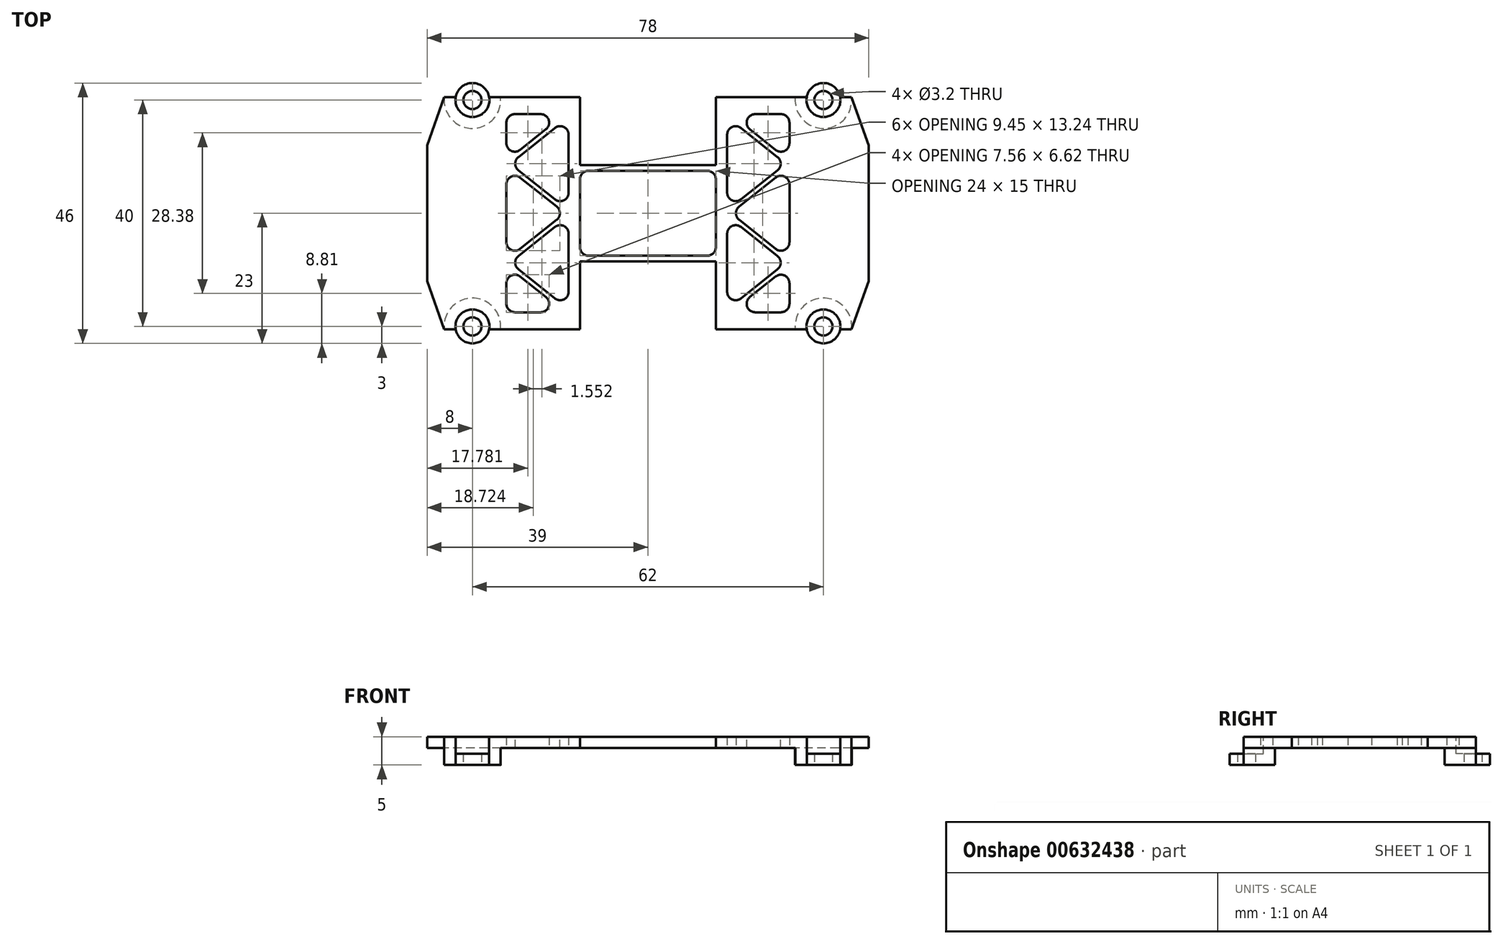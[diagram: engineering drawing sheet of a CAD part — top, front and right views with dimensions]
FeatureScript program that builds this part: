
annotation { "Feature Type Name" : "Feature", "Feature Type Description" : "" }
export const myFeature = defineFeature(function(context is Context, id is Id, definition is map)
    precondition{}
    {
        {
            var Q0;
            Q0=qCreatedBy(makeId("Top.planeOp"),FACE);
            var sketch = newSketch(context, id + "F0", { "sketchPlane" : qUnion([Q0])});
            skLineSegment(sketch, "E0.bottom", {"start": v(-31, 20) * mm, "end": v(31, 20) * mm, "construction": true});
            skLineSegment(sketch, "E0.top", {"start": v(-31, -20) * mm, "end": v(31, -20) * mm, "construction": true});
            skLineSegment(sketch, "E0.left", {"start": v(-31, 20) * mm, "end": v(-31, -20) * mm, "construction": true});
            skLineSegment(sketch, "E0.right", {"start": v(31, 20) * mm, "end": v(31, -20) * mm, "construction": true});
            skCircle(sketch, "E1", {"center": v(-31, 20) * mm, "radius": 1.6 * mm});
            skCircle(sketch, "E2", {"center": v(31, 20) * mm, "radius": 1.6 * mm});
            skCircle(sketch, "E3", {"center": v(31, -20) * mm, "radius": 1.6 * mm});
            skCircle(sketch, "E4", {"center": v(-31, -20) * mm, "radius": 1.6 * mm});
            skLineSegment(sketch, "E5.bottom", {"start": v(-39, 20.5) * mm, "end": v(39, 20.5) * mm});
            skLineSegment(sketch, "E5.top", {"start": v(-39, -20.5) * mm, "end": v(39, -20.5) * mm});
            skLineSegment(sketch, "E5.left", {"start": v(-39, 20.5) * mm, "end": v(-39, -20.5) * mm});
            skLineSegment(sketch, "E5.right", {"start": v(39, 20.5) * mm, "end": v(39, -20.5) * mm});
            skCircle(sketch, "E6", {"center": v(-31, 20) * mm, "radius": 3 * mm});
            skCircle(sketch, "E7", {"center": v(31, 20) * mm, "radius": 3 * mm});
            skCircle(sketch, "E8", {"center": v(31, -20) * mm, "radius": 3 * mm});
            skCircle(sketch, "E9", {"center": v(-31, -20) * mm, "radius": 3 * mm});
            skCircle(sketch, "E10", {"center": v(-31, 20) * mm, "radius": 5 * mm});
            skCircle(sketch, "E11", {"center": v(-31, -20) * mm, "radius": 5 * mm});
            skCircle(sketch, "E12", {"center": v(31, 20) * mm, "radius": 5 * mm});
            skCircle(sketch, "E13", {"center": v(31, -20) * mm, "radius": 5 * mm});
            skLineSegment(sketch, "E14.bottom", {"start": v(-39, 12) * mm, "end": v(-27, 12) * mm});
            skLineSegment(sketch, "E14.top", {"start": v(-39, -12) * mm, "end": v(-27, -12) * mm});
            skLineSegment(sketch, "E14.left", {"start": v(-39, 12) * mm, "end": v(-39, -12) * mm});
            skLineSegment(sketch, "E14.right", {"start": v(-27, 12) * mm, "end": v(-27, -12) * mm});
            skLineSegment(sketch, "E15.bottom", {"start": v(39, 12) * mm, "end": v(27, 12) * mm});
            skLineSegment(sketch, "E15.top", {"start": v(39, -12) * mm, "end": v(27, -12) * mm});
            skLineSegment(sketch, "E15.left", {"start": v(39, 12) * mm, "end": v(39, -12) * mm});
            skLineSegment(sketch, "E15.right", {"start": v(27, 12) * mm, "end": v(27, -12) * mm});
            skLineSegment(sketch, "E16.bottom", {"start": v(-12, 20.5) * mm, "end": v(12, 20.5) * mm});
            skLineSegment(sketch, "E16.top", {"start": v(-12, 8.5) * mm, "end": v(12, 8.5) * mm});
            skLineSegment(sketch, "E16.left", {"start": v(-12, 20.5) * mm, "end": v(-12, 8.5) * mm});
            skLineSegment(sketch, "E16.right", {"start": v(12, 20.5) * mm, "end": v(12, 8.5) * mm});
            skLineSegment(sketch, "E17.bottom", {"start": v(-12, -20.5) * mm, "end": v(12, -20.5) * mm});
            skLineSegment(sketch, "E17.top", {"start": v(-12, -8.5) * mm, "end": v(12, -8.5) * mm});
            skLineSegment(sketch, "E17.left", {"start": v(-12, -20.5) * mm, "end": v(-12, -8.5) * mm});
            skLineSegment(sketch, "E17.right", {"start": v(12, -20.5) * mm, "end": v(12, -8.5) * mm});
            skLineSegment(sketch, "E18.bottom", {"start": v(-12, 7.5) * mm, "end": v(12, 7.5) * mm});
            skLineSegment(sketch, "E18.top", {"start": v(-12, -7.5) * mm, "end": v(12, -7.5) * mm});
            skLineSegment(sketch, "E18.left", {"start": v(-12, 7.5) * mm, "end": v(-12, -7.5) * mm});
            skLineSegment(sketch, "E18.right", {"start": v(12, 7.5) * mm, "end": v(12, -7.5) * mm});
            skPoint(sketch, "E19", {"position": v(-35.97, 20.5) * mm});
            skPoint(sketch, "E20", {"position": v(-35.97, -20.5) * mm});
            skPoint(sketch, "E21", {"position": v(35.97, 20.5) * mm});
            skPoint(sketch, "E22", {"position": v(35.97, -20.5) * mm});
            skLineSegment(sketch, "E23", {"start": v(-35.97, 20.5) * mm, "end": v(-39, 12) * mm});
            skLineSegment(sketch, "E24", {"start": v(-39, -12) * mm, "end": v(-35.97, -20.5) * mm});
            skLineSegment(sketch, "E25", {"start": v(39, 12) * mm, "end": v(35.97, 20.5) * mm});
            skLineSegment(sketch, "E26", {"start": v(39, -12) * mm, "end": v(35.97, -20.5) * mm});
            skLineSegment(sketch, "E27.bottom", {"start": v(-14, 17.5) * mm, "end": v(-25, 17.5) * mm});
            skLineSegment(sketch, "E27.top", {"start": v(-14, -17.5) * mm, "end": v(-25, -17.5) * mm});
            skLineSegment(sketch, "E27.left", {"start": v(-14, 17.5) * mm, "end": v(-14, -17.5) * mm});
            skLineSegment(sketch, "E27.right", {"start": v(-25, 17.5) * mm, "end": v(-25, -17.5) * mm});
            skLineSegment(sketch, "E28.bottom", {"start": v(14, 17.5) * mm, "end": v(25, 17.5) * mm});
            skLineSegment(sketch, "E28.top", {"start": v(14, -17.5) * mm, "end": v(25, -17.5) * mm});
            skLineSegment(sketch, "E28.left", {"start": v(14, 17.5) * mm, "end": v(14, -17.5) * mm});
            skLineSegment(sketch, "E28.right", {"start": v(25, 17.5) * mm, "end": v(25, -17.5) * mm});
            skLineSegment(sketch, "E29", {"start": v(14, 0) * mm, "end": v(25, 8.75) * mm});
            skLineSegment(sketch, "E30", {"start": v(25, 8.75) * mm, "end": v(14, 17.5) * mm});
            skLineSegment(sketch, "E31", {"start": v(14, 0) * mm, "end": v(25, -8.75) * mm});
            skLineSegment(sketch, "E32", {"start": v(25, -8.75) * mm, "end": v(14, -17.5) * mm});
            skLineSegment(sketch, "E33.0", {"start": v(25.64, 8.75) * mm, "end": v(14.25, 17.81) * mm});
            skLineSegment(sketch, "E33.1", {"start": v(14.64, 0) * mm, "end": v(25.64, 8.75) * mm});
            skLineSegment(sketch, "E33.2", {"start": v(14.64, 0) * mm, "end": v(25.64, -8.75) * mm});
            skLineSegment(sketch, "E33.3", {"start": v(25.64, -8.75) * mm, "end": v(14.25, -17.81) * mm});
            skLineSegment(sketch, "E34.0", {"start": v(24.36, 8.75) * mm, "end": v(13.75, 17.19) * mm});
            skLineSegment(sketch, "E34.1", {"start": v(13.36, 0) * mm, "end": v(24.36, 8.75) * mm});
            skLineSegment(sketch, "E34.2", {"start": v(13.36, 0) * mm, "end": v(24.36, -8.75) * mm});
            skLineSegment(sketch, "E34.3", {"start": v(24.36, -8.75) * mm, "end": v(13.75, -17.19) * mm});
            skLineSegment(sketch, "E35", {"start": v(-14, 17.5) * mm, "end": v(-25, 8.75) * mm});
            skLineSegment(sketch, "E36", {"start": v(-25, 8.75) * mm, "end": v(-14, 0) * mm});
            skLineSegment(sketch, "E37", {"start": v(-14, 0) * mm, "end": v(-25, -8.75) * mm});
            skLineSegment(sketch, "E38", {"start": v(-25, -8.75) * mm, "end": v(-14, -17.5) * mm});
            skLineSegment(sketch, "E39.0", {"start": v(-24.36, -8.75) * mm, "end": v(-13.75, -17.19) * mm});
            skLineSegment(sketch, "E39.1", {"start": v(-13.36, 0) * mm, "end": v(-24.36, -8.75) * mm});
            skLineSegment(sketch, "E39.2", {"start": v(-24.36, 8.75) * mm, "end": v(-13.36, 0) * mm});
            skLineSegment(sketch, "E39.3", {"start": v(-13.75, 17.19) * mm, "end": v(-24.36, 8.75) * mm});
            skLineSegment(sketch, "E40.0", {"start": v(-25.64, -8.75) * mm, "end": v(-14.25, -17.81) * mm});
            skLineSegment(sketch, "E40.1", {"start": v(-14.64, 0) * mm, "end": v(-25.64, -8.75) * mm});
            skLineSegment(sketch, "E40.2", {"start": v(-25.64, 8.75) * mm, "end": v(-14.64, 0) * mm});
            skLineSegment(sketch, "E40.3", {"start": v(-14.25, 17.81) * mm, "end": v(-25.64, 8.75) * mm});
            skSolve(sketch);
        }
        {
            var Q0;
            {var subQ0=sQuery(id+"F0.wireOp",EDGE,"E5.top");var subQ1=sQuery(id+"F0.wireOp",EDGE,"E4");var subQ2=makeQuery(id+"F0.imprint","INTERSECT",VERTEX,{"disambiguationData":[OD(0.0)],"derivedFrom":[subQ1,subQ0]});Q0=makeQuery(id+"F0.imprint","IMPRINT",FACE,{"disambiguationData":[TD([[makeQuery(id+"F0.imprint","IMPRINT",EDGE,{"disambiguationData":[TD([[subQ2,-1.0]])],"derivedFrom":subQ1}),-1.0]])]});}
            var Q1;
            {var subQ0=sQuery(id+"F0.wireOp",EDGE,"E5.top");var subQ1=sQuery(id+"F0.wireOp",EDGE,"E4");var subQ2=makeQuery(id+"F0.imprint","INTERSECT",VERTEX,{"disambiguationData":[OD(0.0)],"derivedFrom":[subQ1,subQ0]});Q1=makeQuery(id+"F0.imprint","IMPRINT",FACE,{"disambiguationData":[TD([[makeQuery(id+"F0.imprint","IMPRINT",EDGE,{"disambiguationData":[TD([[subQ2,1.0]])],"derivedFrom":subQ1}),-1.0]])]});}
            var Q2;
            {var subQ0=sQuery(id+"F0.wireOp",EDGE,"E11");var subQ1=sQuery(id+"F0.wireOp",EDGE,"E5.top");var subQ5=makeQuery(id+"F0.imprint","INTERSECT",VERTEX,{"derivedFrom":[subQ1,subQ0]});Q2=makeQuery(id+"F0.imprint","IMPRINT",FACE,{"disambiguationData":[TD([[makeQuery(id+"F0.imprint","IMPRINT",EDGE,{"disambiguationData":[TD([[subQ5,1.0]])],"derivedFrom":subQ1}),1.0]])]});}
            var Q3;
            {var subQ0=sQuery(id+"F0.wireOp",EDGE,"E5.bottom");var subQ1=sQuery(id+"F0.wireOp",EDGE,"E1");var subQ2=makeQuery(id+"F0.imprint","INTERSECT",VERTEX,{"disambiguationData":[OD(0.0)],"derivedFrom":[subQ1,subQ0]});Q3=makeQuery(id+"F0.imprint","IMPRINT",FACE,{"disambiguationData":[TD([[makeQuery(id+"F0.imprint","IMPRINT",EDGE,{"disambiguationData":[TD([[subQ2,1.0]])],"derivedFrom":subQ1}),-1.0]])]});}
            var Q4;
            {var subQ0=sQuery(id+"F0.wireOp",EDGE,"E5.bottom");var subQ1=sQuery(id+"F0.wireOp",EDGE,"E1");var subQ2=makeQuery(id+"F0.imprint","INTERSECT",VERTEX,{"disambiguationData":[OD(0.0)],"derivedFrom":[subQ1,subQ0]});Q4=makeQuery(id+"F0.imprint","IMPRINT",FACE,{"disambiguationData":[TD([[makeQuery(id+"F0.imprint","IMPRINT",EDGE,{"disambiguationData":[TD([[subQ2,-1.0]])],"derivedFrom":subQ1}),-1.0]])]});}
            var Q5;
            {var subQ0=sQuery(id+"F0.wireOp",EDGE,"E5.bottom");var subQ1=sQuery(id+"F0.wireOp",EDGE,"E2");var subQ2=makeQuery(id+"F0.imprint","INTERSECT",VERTEX,{"disambiguationData":[OD(0.0)],"derivedFrom":[subQ1,subQ0]});Q5=makeQuery(id+"F0.imprint","IMPRINT",FACE,{"disambiguationData":[TD([[makeQuery(id+"F0.imprint","IMPRINT",EDGE,{"disambiguationData":[TD([[subQ2,1.0]])],"derivedFrom":subQ1}),-1.0]])]});}
            var Q6;
            {var subQ0=sQuery(id+"F0.wireOp",EDGE,"E5.bottom");var subQ1=sQuery(id+"F0.wireOp",EDGE,"E2");var subQ2=makeQuery(id+"F0.imprint","INTERSECT",VERTEX,{"disambiguationData":[OD(0.0)],"derivedFrom":[subQ1,subQ0]});Q6=makeQuery(id+"F0.imprint","IMPRINT",FACE,{"disambiguationData":[TD([[makeQuery(id+"F0.imprint","IMPRINT",EDGE,{"disambiguationData":[TD([[subQ2,-1.0]])],"derivedFrom":subQ1}),-1.0]])]});}
            var Q7;
            {var subQ0=sQuery(id+"F0.wireOp",EDGE,"E12");var subQ1=sQuery(id+"F0.wireOp",EDGE,"E5.bottom");var subQ2=makeQuery(id+"F0.imprint","INTERSECT",VERTEX,{"derivedFrom":[subQ1,subQ0]});Q7=makeQuery(id+"F0.imprint","IMPRINT",FACE,{"disambiguationData":[TD([[makeQuery(id+"F0.imprint","IMPRINT",EDGE,{"disambiguationData":[TD([[subQ2,-1.0]])],"derivedFrom":subQ1}),-1.0]])]});}
            var Q8;
            {var subQ0=sQuery(id+"F0.wireOp",EDGE,"E10");var subQ1=sQuery(id+"F0.wireOp",EDGE,"E5.bottom");var subQ5=makeQuery(id+"F0.imprint","INTERSECT",VERTEX,{"derivedFrom":[subQ1,subQ0]});Q8=makeQuery(id+"F0.imprint","IMPRINT",FACE,{"disambiguationData":[TD([[makeQuery(id+"F0.imprint","IMPRINT",EDGE,{"disambiguationData":[TD([[subQ5,1.0]])],"derivedFrom":subQ1}),-1.0]])]});}
            var Q9;
            {var subQ0=sQuery(id+"F0.wireOp",EDGE,"E13");var subQ1=sQuery(id+"F0.wireOp",EDGE,"E5.top");var subQ2=makeQuery(id+"F0.imprint","INTERSECT",VERTEX,{"derivedFrom":[subQ1,subQ0]});Q9=makeQuery(id+"F0.imprint","IMPRINT",FACE,{"disambiguationData":[TD([[makeQuery(id+"F0.imprint","IMPRINT",EDGE,{"disambiguationData":[TD([[subQ2,-1.0]])],"derivedFrom":subQ1}),1.0]])]});}
            var Q10;
            {var subQ0=sQuery(id+"F0.wireOp",EDGE,"E5.top");var subQ1=sQuery(id+"F0.wireOp",EDGE,"E3");var subQ2=makeQuery(id+"F0.imprint","INTERSECT",VERTEX,{"disambiguationData":[OD(0.0)],"derivedFrom":[subQ1,subQ0]});Q10=makeQuery(id+"F0.imprint","IMPRINT",FACE,{"disambiguationData":[TD([[makeQuery(id+"F0.imprint","IMPRINT",EDGE,{"disambiguationData":[TD([[subQ2,1.0]])],"derivedFrom":subQ1}),-1.0]])]});}
            var Q11;
            {var subQ0=sQuery(id+"F0.wireOp",EDGE,"E5.top");var subQ1=sQuery(id+"F0.wireOp",EDGE,"E3");var subQ2=makeQuery(id+"F0.imprint","INTERSECT",VERTEX,{"disambiguationData":[OD(0.0)],"derivedFrom":[subQ1,subQ0]});Q11=makeQuery(id+"F0.imprint","IMPRINT",FACE,{"disambiguationData":[TD([[makeQuery(id+"F0.imprint","IMPRINT",EDGE,{"disambiguationData":[TD([[subQ2,-1.0]])],"derivedFrom":subQ1}),-1.0]])]});}
            var Q12;
            Q12=makeQuery(id+"F0.imprint","IMPRINT",FACE,{"disambiguationData":[TD([[makeQuery(id+"F0.imprint","IMPRINT",EDGE,{"derivedFrom":sQuery(id+"F0.wireOp",EDGE,"E14.bottom")}),1.0]])]});
            var Q13;
            Q13=makeQuery(id+"F0.imprint","IMPRINT",FACE,{"disambiguationData":[TD([[makeQuery(id+"F0.imprint","IMPRINT",EDGE,{"derivedFrom":sQuery(id+"F0.wireOp",EDGE,"E15.bottom")}),1.0]])]});
            var Q14;
            Q14=makeQuery(id+"F0.imprint","IMPRINT",FACE,{"disambiguationData":[TD([[makeQuery(id+"F0.imprint","IMPRINT",EDGE,{"derivedFrom":sQuery(id+"F0.wireOp",EDGE,"E14.bottom")}),-1.0]])]});
            var Q15;
            Q15=makeQuery(id+"F0.imprint","IMPRINT",FACE,{"disambiguationData":[TD([[makeQuery(id+"F0.imprint","IMPRINT",EDGE,{"derivedFrom":sQuery(id+"F0.wireOp",EDGE,"E16.bottom")}),-1.0]])]});
            var Q16;
            Q16=makeQuery(id+"F0.imprint","IMPRINT",FACE,{"disambiguationData":[TD([[makeQuery(id+"F0.imprint","IMPRINT",EDGE,{"derivedFrom":sQuery(id+"F0.wireOp",EDGE,"E17.bottom")}),1.0]])]});
            var Q17;
            {var subQ2=sQuery(id+"F0.wireOp",EDGE,"E40.3");var subQ4=sQuery(id+"F0.wireOp",EDGE,"E40.2");var subQ5=makeQuery(id+"F0.imprint","INTERSECT",VERTEX,{"derivedFrom":[subQ4,subQ2]});Q17=makeQuery(id+"F0.imprint","IMPRINT",FACE,{"disambiguationData":[TD([[makeQuery(id+"F0.imprint","IMPRINT",EDGE,{"disambiguationData":[TD([[subQ5,-1.0]])],"derivedFrom":subQ4}),1.0]])]});}
            var Q18;
            {var subQ2=sQuery(id+"F0.wireOp",EDGE,"E40.1");var subQ4=sQuery(id+"F0.wireOp",EDGE,"E40.0");var subQ6=makeQuery(id+"F0.imprint","INTERSECT",VERTEX,{"derivedFrom":[subQ4,subQ2]});Q18=makeQuery(id+"F0.imprint","IMPRINT",FACE,{"disambiguationData":[TD([[makeQuery(id+"F0.imprint","IMPRINT",EDGE,{"disambiguationData":[TD([[subQ6,-1.0]])],"derivedFrom":subQ4}),1.0]])]});}
            var Q19;
            {var subQ0=sQuery(id+"F0.wireOp",EDGE,"E35");Q19=makeQuery(id+"F0.imprint","IMPRINT",FACE,{"disambiguationData":[TD([[makeQuery(id+"F0.imprint","IMPRINT",EDGE,{"derivedFrom":subQ0}),-1.0]])]});}
            var Q20;
            {var subQ1=sQuery(id+"F0.wireOp",EDGE,"E35");Q20=makeQuery(id+"F0.imprint","IMPRINT",FACE,{"disambiguationData":[TD([[makeQuery(id+"F0.imprint","IMPRINT",EDGE,{"derivedFrom":subQ1}),1.0]])]});}
            var Q21;
            {var subQ0=sQuery(id+"F0.wireOp",EDGE,"E36");Q21=makeQuery(id+"F0.imprint","IMPRINT",FACE,{"disambiguationData":[TD([[makeQuery(id+"F0.imprint","IMPRINT",EDGE,{"derivedFrom":subQ0}),-1.0]])]});}
            var Q22;
            {var subQ2=sQuery(id+"F0.wireOp",EDGE,"E39.2");var subQ4=sQuery(id+"F0.wireOp",EDGE,"E39.1");var subQ6=makeQuery(id+"F0.imprint","INTERSECT",VERTEX,{"derivedFrom":[subQ4,subQ2]});Q22=makeQuery(id+"F0.imprint","IMPRINT",FACE,{"disambiguationData":[TD([[makeQuery(id+"F0.imprint","IMPRINT",EDGE,{"disambiguationData":[TD([[subQ6,-1.0]])],"derivedFrom":subQ4}),-1.0]])]});}
            var Q23;
            {var subQ1=sQuery(id+"F0.wireOp",EDGE,"E37");Q23=makeQuery(id+"F0.imprint","IMPRINT",FACE,{"disambiguationData":[TD([[makeQuery(id+"F0.imprint","IMPRINT",EDGE,{"derivedFrom":subQ1}),1.0]])]});}
            var Q24;
            {var subQ0=sQuery(id+"F0.wireOp",EDGE,"E38");Q24=makeQuery(id+"F0.imprint","IMPRINT",FACE,{"disambiguationData":[TD([[makeQuery(id+"F0.imprint","IMPRINT",EDGE,{"derivedFrom":subQ0}),-1.0]])]});}
            var Q25;
            {var subQ4=sQuery(id+"F0.wireOp",EDGE,"E31");Q25=makeQuery(id+"F0.imprint","IMPRINT",FACE,{"disambiguationData":[TD([[makeQuery(id+"F0.imprint","IMPRINT",EDGE,{"derivedFrom":subQ4}),-1.0]])]});}
            var Q26;
            {var subQ6=sQuery(id+"F0.wireOp",EDGE,"E29");Q26=makeQuery(id+"F0.imprint","IMPRINT",FACE,{"disambiguationData":[TD([[makeQuery(id+"F0.imprint","IMPRINT",EDGE,{"derivedFrom":subQ6}),-1.0]])]});}
            var Q27;
            {var subQ6=sQuery(id+"F0.wireOp",EDGE,"E29");Q27=makeQuery(id+"F0.imprint","IMPRINT",FACE,{"disambiguationData":[TD([[makeQuery(id+"F0.imprint","IMPRINT",EDGE,{"derivedFrom":subQ6}),1.0]])]});}
            var Q28;
            {var subQ0=sQuery(id+"F0.wireOp",EDGE,"E30");Q28=makeQuery(id+"F0.imprint","IMPRINT",FACE,{"disambiguationData":[TD([[makeQuery(id+"F0.imprint","IMPRINT",EDGE,{"derivedFrom":subQ0}),-1.0]])]});}
            var Q29;
            {var subQ2=sQuery(id+"F0.wireOp",EDGE,"E33.0");var subQ4=sQuery(id+"F0.wireOp",EDGE,"E33.1");var subQ5=makeQuery(id+"F0.imprint","INTERSECT",VERTEX,{"derivedFrom":[subQ2,subQ4]});Q29=makeQuery(id+"F0.imprint","IMPRINT",FACE,{"disambiguationData":[TD([[makeQuery(id+"F0.imprint","IMPRINT",EDGE,{"disambiguationData":[TD([[subQ5,-1.0]])],"derivedFrom":subQ2}),1.0]])]});}
            var Q30;
            {var subQ2=sQuery(id+"F0.wireOp",EDGE,"E34.1");var subQ4=sQuery(id+"F0.wireOp",EDGE,"E34.2");var subQ6=makeQuery(id+"F0.imprint","INTERSECT",VERTEX,{"derivedFrom":[subQ2,subQ4]});Q30=makeQuery(id+"F0.imprint","IMPRINT",FACE,{"disambiguationData":[TD([[makeQuery(id+"F0.imprint","IMPRINT",EDGE,{"disambiguationData":[TD([[subQ6,-1.0]])],"derivedFrom":subQ2}),-1.0]])]});}
            var Q31;
            {var subQ2=sQuery(id+"F0.wireOp",EDGE,"E33.2");var subQ4=sQuery(id+"F0.wireOp",EDGE,"E33.3");var subQ6=makeQuery(id+"F0.imprint","INTERSECT",VERTEX,{"derivedFrom":[subQ2,subQ4]});Q31=makeQuery(id+"F0.imprint","IMPRINT",FACE,{"disambiguationData":[TD([[makeQuery(id+"F0.imprint","IMPRINT",EDGE,{"disambiguationData":[TD([[subQ6,1.0]])],"derivedFrom":subQ2}),-1.0]])]});}
            var Q32;
            {var subQ0=sQuery(id+"F0.wireOp",EDGE,"E32");Q32=makeQuery(id+"F0.imprint","IMPRINT",FACE,{"disambiguationData":[TD([[makeQuery(id+"F0.imprint","IMPRINT",EDGE,{"derivedFrom":subQ0}),1.0]])]});}
            extrude(context, id + "F1", {"entities" : qUnion([Q0, Q1, Q2, Q3, Q4, Q5, Q6, Q7, Q8, Q9, Q10, Q11, Q12, Q13, Q14, Q15, Q16, Q17, Q18, Q19, Q20, Q21, Q22, Q23, Q24, Q25, Q26, Q27, Q28, Q29, Q30, Q31, Q32]), "depth" : 5 * mm, "offsetDistance" : 25 * mm});
        }
        {
            var Q0;
            Q0=makeQuery(id+"F0.imprint","IMPRINT",FACE,{"disambiguationData":[TD([[makeQuery(id+"F0.imprint","IMPRINT",EDGE,{"derivedFrom":sQuery(id+"F0.wireOp",EDGE,"E14.bottom")}),-1.0]])]});
            var Q1;
            Q1=makeQuery(id+"F0.imprint","IMPRINT",FACE,{"disambiguationData":[TD([[makeQuery(id+"F0.imprint","IMPRINT",EDGE,{"derivedFrom":sQuery(id+"F0.wireOp",EDGE,"E14.bottom")}),1.0]])]});
            var Q2;
            {var subQ2=sQuery(id+"F0.wireOp",EDGE,"E40.3");var subQ4=sQuery(id+"F0.wireOp",EDGE,"E40.2");var subQ5=makeQuery(id+"F0.imprint","INTERSECT",VERTEX,{"derivedFrom":[subQ4,subQ2]});Q2=makeQuery(id+"F0.imprint","IMPRINT",FACE,{"disambiguationData":[TD([[makeQuery(id+"F0.imprint","IMPRINT",EDGE,{"disambiguationData":[TD([[subQ5,-1.0]])],"derivedFrom":subQ4}),1.0]])]});}
            var Q3;
            {var subQ2=sQuery(id+"F0.wireOp",EDGE,"E40.1");var subQ4=sQuery(id+"F0.wireOp",EDGE,"E40.0");var subQ6=makeQuery(id+"F0.imprint","INTERSECT",VERTEX,{"derivedFrom":[subQ4,subQ2]});Q3=makeQuery(id+"F0.imprint","IMPRINT",FACE,{"disambiguationData":[TD([[makeQuery(id+"F0.imprint","IMPRINT",EDGE,{"disambiguationData":[TD([[subQ6,-1.0]])],"derivedFrom":subQ4}),1.0]])]});}
            var Q4;
            {var subQ0=sQuery(id+"F0.wireOp",EDGE,"E35");Q4=makeQuery(id+"F0.imprint","IMPRINT",FACE,{"disambiguationData":[TD([[makeQuery(id+"F0.imprint","IMPRINT",EDGE,{"derivedFrom":subQ0}),-1.0]])]});}
            var Q5;
            {var subQ1=sQuery(id+"F0.wireOp",EDGE,"E35");Q5=makeQuery(id+"F0.imprint","IMPRINT",FACE,{"disambiguationData":[TD([[makeQuery(id+"F0.imprint","IMPRINT",EDGE,{"derivedFrom":subQ1}),1.0]])]});}
            var Q6;
            {var subQ1=sQuery(id+"F0.wireOp",EDGE,"E37");Q6=makeQuery(id+"F0.imprint","IMPRINT",FACE,{"disambiguationData":[TD([[makeQuery(id+"F0.imprint","IMPRINT",EDGE,{"derivedFrom":subQ1}),1.0]])]});}
            var Q7;
            {var subQ0=sQuery(id+"F0.wireOp",EDGE,"E36");Q7=makeQuery(id+"F0.imprint","IMPRINT",FACE,{"disambiguationData":[TD([[makeQuery(id+"F0.imprint","IMPRINT",EDGE,{"derivedFrom":subQ0}),-1.0]])]});}
            var Q8;
            {var subQ2=sQuery(id+"F0.wireOp",EDGE,"E39.2");var subQ4=sQuery(id+"F0.wireOp",EDGE,"E39.1");var subQ6=makeQuery(id+"F0.imprint","INTERSECT",VERTEX,{"derivedFrom":[subQ4,subQ2]});Q8=makeQuery(id+"F0.imprint","IMPRINT",FACE,{"disambiguationData":[TD([[makeQuery(id+"F0.imprint","IMPRINT",EDGE,{"disambiguationData":[TD([[subQ6,-1.0]])],"derivedFrom":subQ4}),-1.0]])]});}
            var Q9;
            {var subQ0=sQuery(id+"F0.wireOp",EDGE,"E38");Q9=makeQuery(id+"F0.imprint","IMPRINT",FACE,{"disambiguationData":[TD([[makeQuery(id+"F0.imprint","IMPRINT",EDGE,{"derivedFrom":subQ0}),-1.0]])]});}
            var Q10;
            Q10=makeQuery(id+"F0.imprint","IMPRINT",FACE,{"disambiguationData":[TD([[makeQuery(id+"F0.imprint","IMPRINT",EDGE,{"derivedFrom":sQuery(id+"F0.wireOp",EDGE,"E16.bottom")}),-1.0]])]});
            var Q11;
            Q11=makeQuery(id+"F0.imprint","IMPRINT",FACE,{"disambiguationData":[TD([[makeQuery(id+"F0.imprint","IMPRINT",EDGE,{"derivedFrom":sQuery(id+"F0.wireOp",EDGE,"E17.bottom")}),1.0]])]});
            var Q12;
            Q12=makeQuery(id+"F0.imprint","IMPRINT",FACE,{"disambiguationData":[TD([[makeQuery(id+"F0.imprint","IMPRINT",EDGE,{"derivedFrom":sQuery(id+"F0.wireOp",EDGE,"E15.bottom")}),1.0]])]});
            var Q13;
            {var subQ2=sQuery(id+"F0.wireOp",EDGE,"E33.0");var subQ4=sQuery(id+"F0.wireOp",EDGE,"E33.1");var subQ5=makeQuery(id+"F0.imprint","INTERSECT",VERTEX,{"derivedFrom":[subQ2,subQ4]});Q13=makeQuery(id+"F0.imprint","IMPRINT",FACE,{"disambiguationData":[TD([[makeQuery(id+"F0.imprint","IMPRINT",EDGE,{"disambiguationData":[TD([[subQ5,-1.0]])],"derivedFrom":subQ2}),1.0]])]});}
            var Q14;
            {var subQ2=sQuery(id+"F0.wireOp",EDGE,"E33.2");var subQ4=sQuery(id+"F0.wireOp",EDGE,"E33.3");var subQ6=makeQuery(id+"F0.imprint","INTERSECT",VERTEX,{"derivedFrom":[subQ2,subQ4]});Q14=makeQuery(id+"F0.imprint","IMPRINT",FACE,{"disambiguationData":[TD([[makeQuery(id+"F0.imprint","IMPRINT",EDGE,{"disambiguationData":[TD([[subQ6,1.0]])],"derivedFrom":subQ2}),-1.0]])]});}
            var Q15;
            {var subQ0=sQuery(id+"F0.wireOp",EDGE,"E30");Q15=makeQuery(id+"F0.imprint","IMPRINT",FACE,{"disambiguationData":[TD([[makeQuery(id+"F0.imprint","IMPRINT",EDGE,{"derivedFrom":subQ0}),-1.0]])]});}
            var Q16;
            {var subQ6=sQuery(id+"F0.wireOp",EDGE,"E29");Q16=makeQuery(id+"F0.imprint","IMPRINT",FACE,{"disambiguationData":[TD([[makeQuery(id+"F0.imprint","IMPRINT",EDGE,{"derivedFrom":subQ6}),1.0]])]});}
            var Q17;
            {var subQ2=sQuery(id+"F0.wireOp",EDGE,"E34.1");var subQ4=sQuery(id+"F0.wireOp",EDGE,"E34.2");var subQ6=makeQuery(id+"F0.imprint","INTERSECT",VERTEX,{"derivedFrom":[subQ2,subQ4]});Q17=makeQuery(id+"F0.imprint","IMPRINT",FACE,{"disambiguationData":[TD([[makeQuery(id+"F0.imprint","IMPRINT",EDGE,{"disambiguationData":[TD([[subQ6,-1.0]])],"derivedFrom":subQ2}),-1.0]])]});}
            var Q18;
            {var subQ4=sQuery(id+"F0.wireOp",EDGE,"E31");Q18=makeQuery(id+"F0.imprint","IMPRINT",FACE,{"disambiguationData":[TD([[makeQuery(id+"F0.imprint","IMPRINT",EDGE,{"derivedFrom":subQ4}),-1.0]])]});}
            var Q19;
            {var subQ0=sQuery(id+"F0.wireOp",EDGE,"E32");Q19=makeQuery(id+"F0.imprint","IMPRINT",FACE,{"disambiguationData":[TD([[makeQuery(id+"F0.imprint","IMPRINT",EDGE,{"derivedFrom":subQ0}),1.0]])]});}
            var Q20;
            {var subQ6=sQuery(id+"F0.wireOp",EDGE,"E29");Q20=makeQuery(id+"F0.imprint","IMPRINT",FACE,{"disambiguationData":[TD([[makeQuery(id+"F0.imprint","IMPRINT",EDGE,{"derivedFrom":subQ6}),-1.0]])]});}
            extrude(context, id + "F2", {"entities" : qUnion([Q0, Q1, Q2, Q3, Q4, Q5, Q6, Q7, Q8, Q9, Q10, Q11, Q12, Q13, Q14, Q15, Q16, Q17, Q18, Q19, Q20]), "operationType" : NewBodyOperationType.REMOVE, "depth" : 3 * mm, "offsetDistance" : 25 * mm});
        }
        {
            var Q0;
            Q0=makeQuery(id+"F1.opExtrude","CAP_FACE",FACE,{"disambiguationData":[OSD([sQuery(id+"F0.wireOp",EDGE,"E1"),sQuery(id+"F0.wireOp",EDGE,"E2"),sQuery(id+"F0.wireOp",EDGE,"E3"),sQuery(id+"F0.wireOp",EDGE,"E4"),sQuery(id+"F0.wireOp",EDGE,"E5.bottom"),sQuery(id+"F0.wireOp",EDGE,"E5.top"),sQuery(id+"F0.wireOp",EDGE,"E6"),sQuery(id+"F0.wireOp",EDGE,"E7"),sQuery(id+"F0.wireOp",EDGE,"E8"),sQuery(id+"F0.wireOp",EDGE,"E9"),sQuery(id+"F0.wireOp",EDGE,"E14.left"),sQuery(id+"F0.wireOp",EDGE,"E15.left"),sQuery(id+"F0.wireOp",EDGE,"E16.bottom"),sQuery(id+"F0.wireOp",EDGE,"E17.bottom"),sQuery(id+"F0.wireOp",EDGE,"E18.bottom"),sQuery(id+"F0.wireOp",EDGE,"E18.top"),sQuery(id+"F0.wireOp",EDGE,"E18.left"),sQuery(id+"F0.wireOp",EDGE,"E18.right"),sQuery(id+"F0.wireOp",EDGE,"E23"),sQuery(id+"F0.wireOp",EDGE,"E24"),sQuery(id+"F0.wireOp",EDGE,"E25"),sQuery(id+"F0.wireOp",EDGE,"E26"),sQuery(id+"F0.wireOp",EDGE,"E27.bottom"),sQuery(id+"F0.wireOp",EDGE,"E27.top"),sQuery(id+"F0.wireOp",EDGE,"E27.left"),sQuery(id+"F0.wireOp",EDGE,"E27.right"),sQuery(id+"F0.wireOp",EDGE,"E28.bottom"),sQuery(id+"F0.wireOp",EDGE,"E28.top"),sQuery(id+"F0.wireOp",EDGE,"E28.left"),sQuery(id+"F0.wireOp",EDGE,"E28.right"),sQuery(id+"F0.wireOp",EDGE,"E33.0"),sQuery(id+"F0.wireOp",EDGE,"E33.1"),sQuery(id+"F0.wireOp",EDGE,"E33.2"),sQuery(id+"F0.wireOp",EDGE,"E33.3"),sQuery(id+"F0.wireOp",EDGE,"E34.0"),sQuery(id+"F0.wireOp",EDGE,"E34.1"),sQuery(id+"F0.wireOp",EDGE,"E34.2"),sQuery(id+"F0.wireOp",EDGE,"E34.3"),sQuery(id+"F0.wireOp",EDGE,"E39.0"),sQuery(id+"F0.wireOp",EDGE,"E39.1"),sQuery(id+"F0.wireOp",EDGE,"E39.2"),sQuery(id+"F0.wireOp",EDGE,"E39.3"),sQuery(id+"F0.wireOp",EDGE,"E40.0"),sQuery(id+"F0.wireOp",EDGE,"E40.1"),sQuery(id+"F0.wireOp",EDGE,"E40.2"),sQuery(id+"F0.wireOp",EDGE,"E40.3")])],"isStart":false});
            var sketch = newSketch(context, id + "F3", { "sketchPlane" : qUnion([Q0])});
            skCircle(sketch, "E41", {"center": v(31, 20) * mm, "radius": 3 * mm});
            skCircle(sketch, "E42", {"center": v(31, -20) * mm, "radius": 3 * mm});
            skCircle(sketch, "E43", {"center": v(-31, -20) * mm, "radius": 3 * mm});
            skCircle(sketch, "E44", {"center": v(-31, 20) * mm, "radius": 3 * mm});
            skSolve(sketch);
        }
        {
            var Q0;
            Q0=makeQuery(id+"F3.imprint","IMPRINT",FACE,{"disambiguationData":[TD([[makeQuery(id+"F3.imprint","IMPRINT",EDGE,{"derivedFrom":makeQuery(id+"F1.opExtrude","CAP_EDGE",EDGE,{"disambiguationData":[OSD([sQuery(id+"F0.wireOp",EDGE,"E1")])],"isStart":false})}),-1.0]])]});
            var Q1;
            Q1=makeQuery(id+"F3.imprint","IMPRINT",FACE,{"disambiguationData":[TD([[makeQuery(id+"F3.imprint","IMPRINT",EDGE,{"derivedFrom":makeQuery(id+"F1.opExtrude","CAP_EDGE",EDGE,{"disambiguationData":[OSD([sQuery(id+"F0.wireOp",EDGE,"E4")])],"isStart":false})}),-1.0]])]});
            var Q2;
            Q2=makeQuery(id+"F3.imprint","IMPRINT",FACE,{"disambiguationData":[TD([[makeQuery(id+"F3.imprint","IMPRINT",EDGE,{"derivedFrom":makeQuery(id+"F1.opExtrude","CAP_EDGE",EDGE,{"disambiguationData":[OSD([sQuery(id+"F0.wireOp",EDGE,"E3")])],"isStart":false})}),-1.0]])]});
            var Q3;
            Q3=makeQuery(id+"F3.imprint","IMPRINT",FACE,{"disambiguationData":[TD([[makeQuery(id+"F3.imprint","IMPRINT",EDGE,{"derivedFrom":makeQuery(id+"F1.opExtrude","CAP_EDGE",EDGE,{"disambiguationData":[OSD([sQuery(id+"F0.wireOp",EDGE,"E2")])],"isStart":false})}),-1.0]])]});
            extrude(context, id + "F4", {"entities" : qUnion([Q0, Q1, Q2, Q3]), "operationType" : NewBodyOperationType.REMOVE, "oppositeDirection" : true, "depth" : 3 * mm, "offsetDistance" : 25 * mm});
        }
        {
            var Q0;
            Q0=makeQuery(id+"F1.opExtrude","SWEPT_EDGE",EDGE,{"disambiguationData":[OSD([sQuery(id+"F0.wireOp",EDGE,"E28.top"),sQuery(id+"F0.wireOp",EDGE,"E28.right")])]});
            var Q1;
            Q1=makeQuery(id+"F1.opExtrude","SWEPT_EDGE",EDGE,{"disambiguationData":[OSD([sQuery(id+"F0.wireOp",EDGE,"E28.top"),sQuery(id+"F0.wireOp",EDGE,"E33.3")])]});
            var Q2;
            Q2=makeQuery(id+"F1.opExtrude","SWEPT_EDGE",EDGE,{"disambiguationData":[OSD([sQuery(id+"F0.wireOp",EDGE,"E28.right"),sQuery(id+"F0.wireOp",EDGE,"E33.3")])]});
            var Q3;
            Q3=makeQuery(id+"F1.opExtrude","SWEPT_EDGE",EDGE,{"disambiguationData":[OSD([sQuery(id+"F0.wireOp",EDGE,"E34.2"),sQuery(id+"F0.wireOp",EDGE,"E34.3")])]});
            var Q4;
            Q4=makeQuery(id+"F1.opExtrude","SWEPT_EDGE",EDGE,{"disambiguationData":[OSD([sQuery(id+"F0.wireOp",EDGE,"E28.left"),sQuery(id+"F0.wireOp",EDGE,"E34.3")])]});
            var Q5;
            Q5=makeQuery(id+"F1.opExtrude","SWEPT_EDGE",EDGE,{"disambiguationData":[OSD([sQuery(id+"F0.wireOp",EDGE,"E28.left"),sQuery(id+"F0.wireOp",EDGE,"E34.2")])]});
            var Q6;
            Q6=makeQuery(id+"F1.opExtrude","SWEPT_EDGE",EDGE,{"disambiguationData":[OSD([sQuery(id+"F0.wireOp",EDGE,"E28.right"),sQuery(id+"F0.wireOp",EDGE,"E33.2")])]});
            var Q7;
            Q7=makeQuery(id+"F1.opExtrude","SWEPT_EDGE",EDGE,{"disambiguationData":[OSD([sQuery(id+"F0.wireOp",EDGE,"E33.1"),sQuery(id+"F0.wireOp",EDGE,"E33.2")])]});
            var Q8;
            Q8=makeQuery(id+"F1.opExtrude","SWEPT_EDGE",EDGE,{"disambiguationData":[OSD([sQuery(id+"F0.wireOp",EDGE,"E28.right"),sQuery(id+"F0.wireOp",EDGE,"E33.1")])]});
            var Q9;
            Q9=makeQuery(id+"F1.opExtrude","SWEPT_EDGE",EDGE,{"disambiguationData":[OSD([sQuery(id+"F0.wireOp",EDGE,"E28.left"),sQuery(id+"F0.wireOp",EDGE,"E34.1")])]});
            var Q10;
            Q10=makeQuery(id+"F1.opExtrude","SWEPT_EDGE",EDGE,{"disambiguationData":[OSD([sQuery(id+"F0.wireOp",EDGE,"E34.0"),sQuery(id+"F0.wireOp",EDGE,"E34.1")])]});
            var Q11;
            Q11=makeQuery(id+"F1.opExtrude","SWEPT_EDGE",EDGE,{"disambiguationData":[OSD([sQuery(id+"F0.wireOp",EDGE,"E28.left"),sQuery(id+"F0.wireOp",EDGE,"E34.0")])]});
            var Q12;
            Q12=makeQuery(id+"F1.opExtrude","SWEPT_EDGE",EDGE,{"disambiguationData":[OSD([sQuery(id+"F0.wireOp",EDGE,"E28.right"),sQuery(id+"F0.wireOp",EDGE,"E33.0")])]});
            var Q13;
            Q13=makeQuery(id+"F1.opExtrude","SWEPT_EDGE",EDGE,{"disambiguationData":[OSD([sQuery(id+"F0.wireOp",EDGE,"E28.bottom"),sQuery(id+"F0.wireOp",EDGE,"E33.0")])]});
            var Q14;
            Q14=makeQuery(id+"F1.opExtrude","SWEPT_EDGE",EDGE,{"disambiguationData":[OSD([sQuery(id+"F0.wireOp",EDGE,"E28.bottom"),sQuery(id+"F0.wireOp",EDGE,"E28.right")])]});
            var Q15;
            Q15=makeQuery(id+"F1.opExtrude","SWEPT_EDGE",EDGE,{"disambiguationData":[OSD([sQuery(id+"F0.wireOp",EDGE,"E27.bottom"),sQuery(id+"F0.wireOp",EDGE,"E27.right")])]});
            var Q16;
            Q16=makeQuery(id+"F1.opExtrude","SWEPT_EDGE",EDGE,{"disambiguationData":[OSD([sQuery(id+"F0.wireOp",EDGE,"E27.right"),sQuery(id+"F0.wireOp",EDGE,"E40.2")])]});
            var Q17;
            Q17=makeQuery(id+"F1.opExtrude","SWEPT_EDGE",EDGE,{"disambiguationData":[OSD([sQuery(id+"F0.wireOp",EDGE,"E27.right"),sQuery(id+"F0.wireOp",EDGE,"E40.0")])]});
            var Q18;
            Q18=makeQuery(id+"F1.opExtrude","SWEPT_EDGE",EDGE,{"disambiguationData":[OSD([sQuery(id+"F0.wireOp",EDGE,"E27.top"),sQuery(id+"F0.wireOp",EDGE,"E27.right")])]});
            var Q19;
            Q19=makeQuery(id+"F1.opExtrude","SWEPT_EDGE",EDGE,{"disambiguationData":[OSD([sQuery(id+"F0.wireOp",EDGE,"E27.right"),sQuery(id+"F0.wireOp",EDGE,"E40.1")])]});
            var Q20;
            Q20=makeQuery(id+"F1.opExtrude","SWEPT_EDGE",EDGE,{"disambiguationData":[OSD([sQuery(id+"F0.wireOp",EDGE,"E27.right"),sQuery(id+"F0.wireOp",EDGE,"E40.3")])]});
            var Q21;
            Q21=makeQuery(id+"F1.opExtrude","SWEPT_EDGE",EDGE,{"disambiguationData":[OSD([sQuery(id+"F0.wireOp",EDGE,"E39.2"),sQuery(id+"F0.wireOp",EDGE,"E39.3")])]});
            var Q22;
            Q22=makeQuery(id+"F1.opExtrude","SWEPT_EDGE",EDGE,{"disambiguationData":[OSD([sQuery(id+"F0.wireOp",EDGE,"E39.0"),sQuery(id+"F0.wireOp",EDGE,"E39.1")])]});
            var Q23;
            Q23=makeQuery(id+"F1.opExtrude","SWEPT_EDGE",EDGE,{"disambiguationData":[OSD([sQuery(id+"F0.wireOp",EDGE,"E40.1"),sQuery(id+"F0.wireOp",EDGE,"E40.2")])]});
            var Q24;
            Q24=makeQuery(id+"F1.opExtrude","SWEPT_EDGE",EDGE,{"disambiguationData":[OSD([sQuery(id+"F0.wireOp",EDGE,"E27.top"),sQuery(id+"F0.wireOp",EDGE,"E40.0")])]});
            var Q25;
            Q25=makeQuery(id+"F1.opExtrude","SWEPT_EDGE",EDGE,{"disambiguationData":[OSD([sQuery(id+"F0.wireOp",EDGE,"E27.bottom"),sQuery(id+"F0.wireOp",EDGE,"E40.3")])]});
            var Q26;
            Q26=makeQuery(id+"F1.opExtrude","SWEPT_EDGE",EDGE,{"disambiguationData":[OSD([sQuery(id+"F0.wireOp",EDGE,"E27.left"),sQuery(id+"F0.wireOp",EDGE,"E39.3")])]});
            var Q27;
            Q27=makeQuery(id+"F1.opExtrude","SWEPT_EDGE",EDGE,{"disambiguationData":[OSD([sQuery(id+"F0.wireOp",EDGE,"E27.left"),sQuery(id+"F0.wireOp",EDGE,"E39.1")])]});
            var Q28;
            Q28=makeQuery(id+"F1.opExtrude","SWEPT_EDGE",EDGE,{"disambiguationData":[OSD([sQuery(id+"F0.wireOp",EDGE,"E27.left"),sQuery(id+"F0.wireOp",EDGE,"E39.2")])]});
            var Q29;
            Q29=makeQuery(id+"F1.opExtrude","SWEPT_EDGE",EDGE,{"disambiguationData":[OSD([sQuery(id+"F0.wireOp",EDGE,"E27.left"),sQuery(id+"F0.wireOp",EDGE,"E39.0")])]});
            var Q30;
            Q30=makeQuery(id+"F1.opExtrude","SWEPT_EDGE",EDGE,{"disambiguationData":[OSD([sQuery(id+"F0.wireOp",EDGE,"E18.top"),sQuery(id+"F0.wireOp",EDGE,"E18.left")])]});
            var Q31;
            Q31=makeQuery(id+"F1.opExtrude","SWEPT_EDGE",EDGE,{"disambiguationData":[OSD([sQuery(id+"F0.wireOp",EDGE,"E18.top"),sQuery(id+"F0.wireOp",EDGE,"E18.right")])]});
            var Q32;
            Q32=makeQuery(id+"F1.opExtrude","SWEPT_EDGE",EDGE,{"disambiguationData":[OSD([sQuery(id+"F0.wireOp",EDGE,"E18.bottom"),sQuery(id+"F0.wireOp",EDGE,"E18.right")])]});
            var Q33;
            Q33=makeQuery(id+"F1.opExtrude","SWEPT_EDGE",EDGE,{"disambiguationData":[OSD([sQuery(id+"F0.wireOp",EDGE,"E18.bottom"),sQuery(id+"F0.wireOp",EDGE,"E18.left")])]});
            fillet(context, id + "F5", {"entities" : qUnion([Q0, Q1, Q2, Q3, Q4, Q5, Q6, Q7, Q8, Q9, Q10, Q11, Q12, Q13, Q14, Q15, Q16, Q17, Q18, Q19, Q20, Q21, Q22, Q23, Q24, Q25, Q26, Q27, Q28, Q29, Q30, Q31, Q32, Q33]), "radius" : 1.5 * mm, "tangentPropagation" : true, "allowEdgeOverflow" : false});
        }
    });
